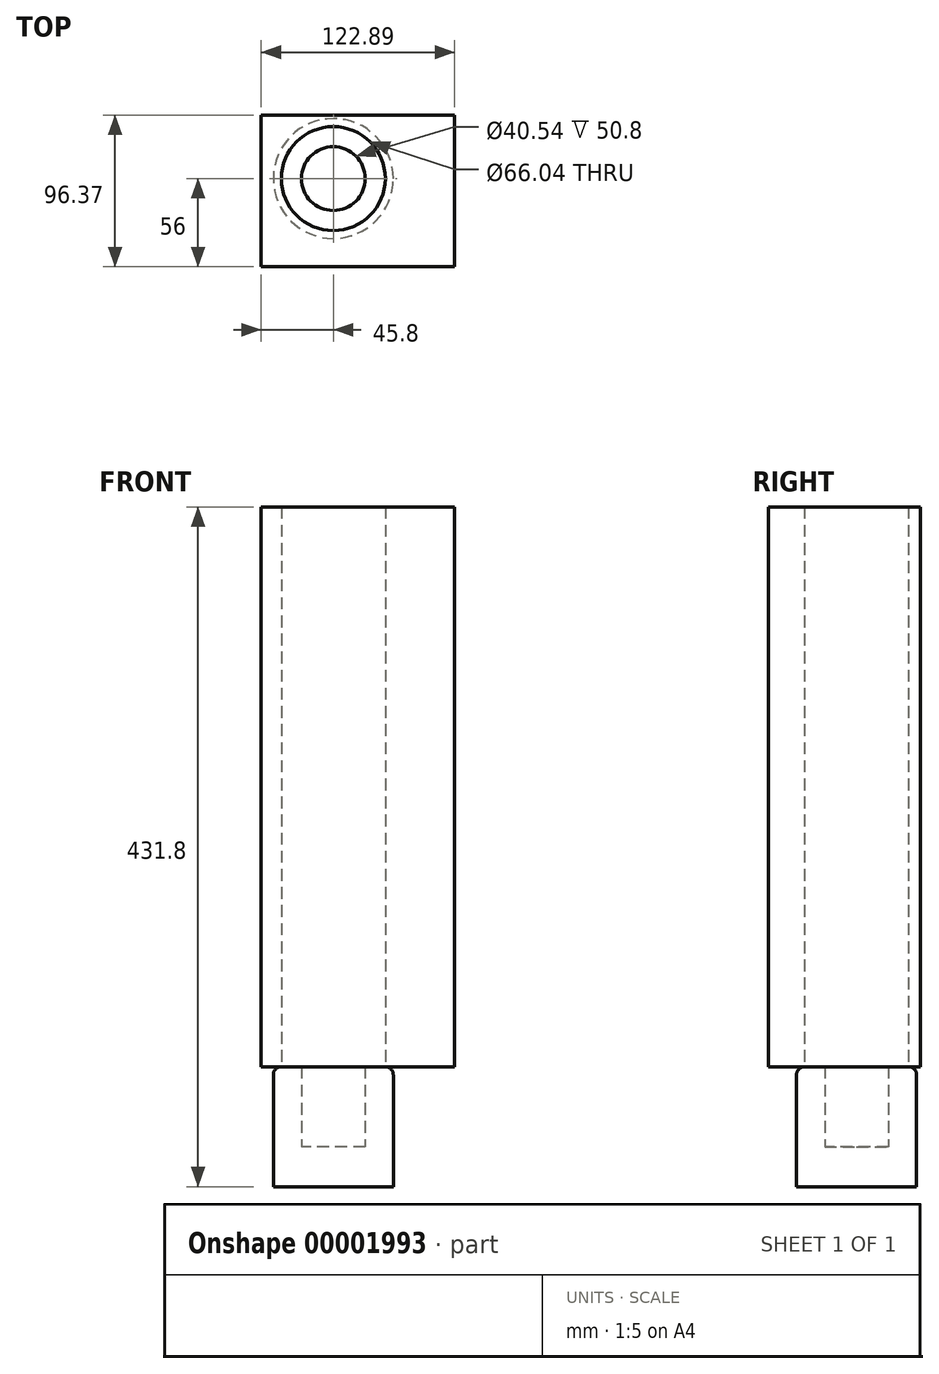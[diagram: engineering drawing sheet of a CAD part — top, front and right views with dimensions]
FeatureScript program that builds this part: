
annotation { "Feature Type Name" : "Feature", "Feature Type Description" : "" }
export const myFeature = defineFeature(function(context is Context, id is Id, definition is map)
    precondition{}
    {
        {
            var Q0;
            Q0=qCreatedBy(makeId("Top.planeOp"),FACE);
            var sketch = newSketch(context, id + "F0", { "sketchPlane" : qUnion([Q0])});
            skCircle(sketch, "E0", {"center": v(0, 0) * mm, "radius": 38.1 * mm});
            skSolve(sketch);
        }
        {
            var Q0;
            Q0=makeQuery(id+"F0.imprint","IMPRINT",FACE,{"disambiguationData":[TD([[makeQuery(id+"F0.imprint","IMPRINT",EDGE,{"derivedFrom":sQuery(id+"F0.wireOp",EDGE,"E0")}),1.0]])]});
            extrude(context, id + "F1", {"entities" : qUnion([Q0]), "depth" : 25.4 * mm});
        }
        {
            var Q0;
            Q0=makeQuery(id+"F1.opExtrude","CAP_FACE",FACE,{"disambiguationData":[OSD([sQuery(id+"F0.wireOp",EDGE,"E0")])],"isStart":false});
            var sketch = newSketch(context, id + "F2", { "sketchPlane" : qUnion([Q0])});
            skCircle(sketch, "E1", {"center": v(0, 0) * mm, "radius": 20.27 * mm});
            skSolve(sketch);
        }
        {
            var Q0;
            Q0=makeQuery(id+"F2.imprint","IMPRINT",FACE,{"disambiguationData":[TD([[makeQuery(id+"F2.imprint","IMPRINT",EDGE,{"derivedFrom":sQuery(id+"F2.wireOp",EDGE,"E1")}),-1.0]])]});
            extrude(context, id + "F3", {"entities" : qUnion([Q0]), "operationType" : NewBodyOperationType.ADD, "depth" : 50.8 * mm});
        }
        {
            var Q0;
            Q0=makeQuery(id+"F3.opExtrude","CAP_EDGE",EDGE,{"disambiguationData":[OSD([sQuery(id+"F0.wireOp",EDGE,"E0")])],"isStart":false});
            fillet(context, id + "F4", {"entities" : qUnion([Q0]), "radius" : 5.08 * mm, "tangentPropagation" : true, "allowEdgeOverflow" : false});
        }
        {
            var Q0;
            Q0=makeQuery(id+"F3.opExtrude","CAP_FACE",FACE,{"disambiguationData":[OSD([sQuery(id+"F0.wireOp",EDGE,"E0"),sQuery(id+"F2.wireOp",EDGE,"E1")])],"isStart":false});
            var sketch = newSketch(context, id + "F5", { "sketchPlane" : qUnion([Q0])});
            skLineSegment(sketch, "E2.bottom", {"start": v(-45.8, 40.37) * mm, "end": v(77.09, 40.37) * mm});
            skLineSegment(sketch, "E2.top", {"start": v(-45.8, -56) * mm, "end": v(77.09, -56) * mm});
            skLineSegment(sketch, "E2.left", {"start": v(-45.8, 40.37) * mm, "end": v(-45.8, -56) * mm});
            skLineSegment(sketch, "E2.right", {"start": v(77.09, 40.37) * mm, "end": v(77.09, -56) * mm});
            skSolve(sketch);
        }
        {
            var Q0;
            Q0=makeQuery(id+"F5.imprint","IMPRINT",FACE,{"disambiguationData":[TD([[makeQuery(id+"F5.imprint","IMPRINT",EDGE,{"derivedFrom":sQuery(id+"F5.wireOp",EDGE,"E2.bottom")}),-1.0]])]});
            extrude(context, id + "F6", {"entities" : qUnion([Q0]), "depth" : 355.6 * mm});
        }
    });
